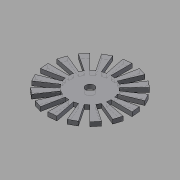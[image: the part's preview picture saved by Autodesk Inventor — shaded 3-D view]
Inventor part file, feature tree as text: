
AUTODESK INVENTOR PART (.ipt)
format: ipt  version: 2015 (Build 190159000, 159)  size: 173,056 bytes
history: native  units: in
note: dims shown in document units (in); Inventor stores cm internally (conversion verified against a paired STEP export)
features: other x3, sketch x1
ambient origin geometry x8: Origin, YZ Plane, XZ Plane, XY Plane, X Axis, Y Axis, Z Axis, Center Point
bodies: Solid1 (feature_tree)
feature tree (4):
  other  "encoder.ipt"
  other  "Solid2::encoder.ipt"
  other  "TaggingFeature1"
  sketch  "Sketch1"  dims[d0=0.3937in]
